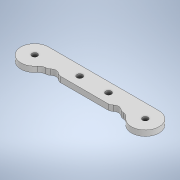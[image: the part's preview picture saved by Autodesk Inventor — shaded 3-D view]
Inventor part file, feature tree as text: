
AUTODESK INVENTOR PART (.ipt)
format: ipt  version: 2020 (Build 240168000, 168)  size: 162,816 bytes
history: native  units: in
note: dims shown in document units (in); Inventor stores cm internally (conversion verified against a paired STEP export)
features: fillet x3, extrude x1, sketch x1
ambient origin geometry x8: Origin, YZ Plane, XZ Plane, XY Plane, X Axis, Y Axis, Z Axis, Center Point
bodies: Solid1 (feature_tree)
feature tree (5):
  extrude  "Extrusion1"  Depth=0.3937in
  fillet  "Fillet1"  Radius=0.4151in
  fillet  "Fillet2"  Radius=0.122in
  fillet  "Fillet3"  Radius=0.122in
  sketch  "Sketch1"  dims[d0=0.3937in d1=0.3937in d2=0.5906in d3=0.5906in d4=0.122in d5=0.122in d6=0.122in d7=0.1181in d8=0.0in d9=0.3937in d13=0.4151in d14=0.122in d15=0.122in d16=0.2461in d17=0.2461in d18=0.1181in d19=0.1575in]
